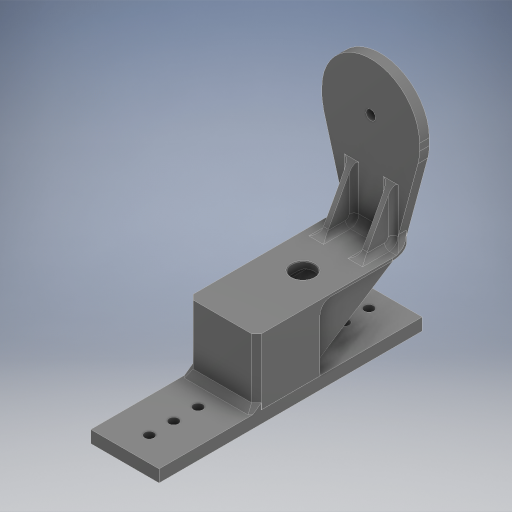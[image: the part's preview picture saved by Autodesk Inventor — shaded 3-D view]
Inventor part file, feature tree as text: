
AUTODESK INVENTOR PART (.ipt)
format: ipt  version: 2024.2 (Build 282272000, 272)  size: 473,088 bytes
history: native  units: in
note: dims shown in document units (in); Inventor stores cm internally (conversion verified against a paired STEP export)
features: sketch x3, extrude x2, chamfer x1, projected_geometry x1, other x1
ambient origin geometry x8: Origin, YZ Plane, XZ Plane, XY Plane, X Axis, Y Axis, Z Axis, Center Point
bodies: Solid1 (feature_tree)
feature tree (8):
  extrude  "Extrusion1"  Depth=0.25in
  sketch  "Sketch2"  dims[d4=0.125in d5=0.125in d6=45.0deg d7=0.196in]
  chamfer  "Chamfer1"  Distance=0.25in
  extrude  "Extrusion2"  Depth=0.196in
  sketch  "Sketch1"  dims[d0=2.5in d1=5.0in d2=0.25in d3=0.0in]
  projected_geometry  "Projected Loop1"
  sketch  "Sketch3"  dims[d8=0.5in d9=3.937in d11=0.5in d12=0.3937in d14=1.0in d16=0.9375in d17=0.0in]
  other  "Main camera mount"
